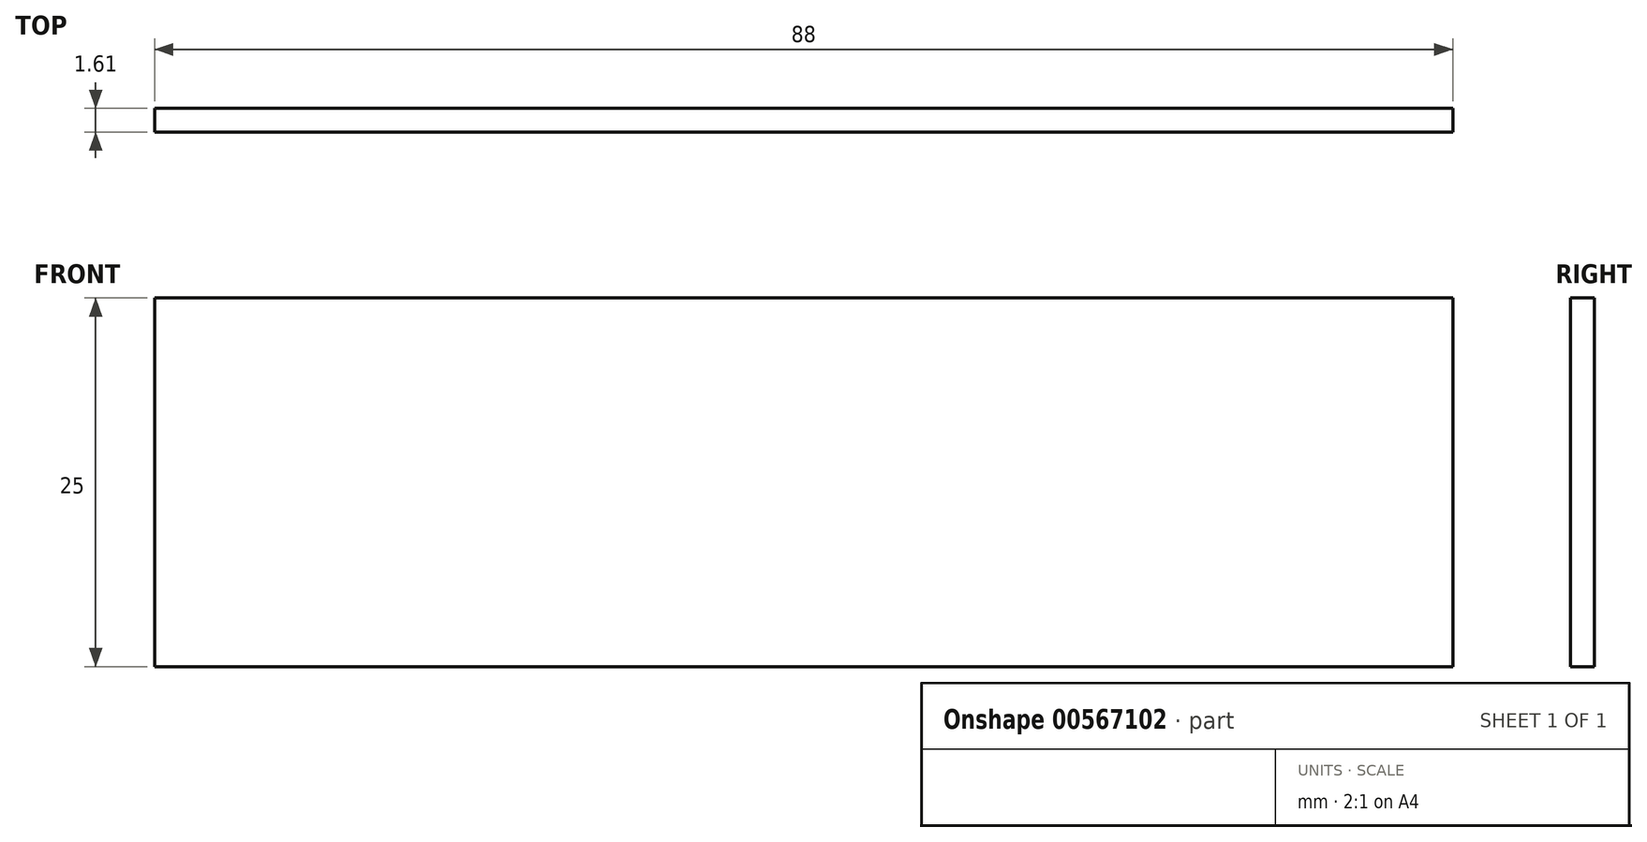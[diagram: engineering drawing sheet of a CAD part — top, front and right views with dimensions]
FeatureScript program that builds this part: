
annotation { "Feature Type Name" : "Feature", "Feature Type Description" : "" }
export const myFeature = defineFeature(function(context is Context, id is Id, definition is map)
    precondition{}
    {
        {
            var Q0;
            Q0=qCreatedBy(makeId("Front.planeOp"),FACE);
            var sketch = newSketch(context, id + "F0", { "sketchPlane" : qUnion([Q0])});
            skLineSegment(sketch, "E0.bottom", {"start": v(-58.79, 63.95) * mm, "end": v(29.21, 63.95) * mm});
            skLineSegment(sketch, "E0.top", {"start": v(-58.79, 38.95) * mm, "end": v(29.21, 38.95) * mm});
            skLineSegment(sketch, "E0.left", {"start": v(-58.79, 63.95) * mm, "end": v(-58.79, 38.95) * mm});
            skLineSegment(sketch, "E0.right", {"start": v(29.21, 63.95) * mm, "end": v(29.21, 38.95) * mm});
            skSolve(sketch);
        }
        {
            var Q0;
            Q0 = qSketchRegion(id + "F0", true);
            extrude(context, id + "F1", {"entities" : qUnion([Q0]), "depth" : 1.61 * mm, "offsetDistance" : 25 * mm});
        }
    });
